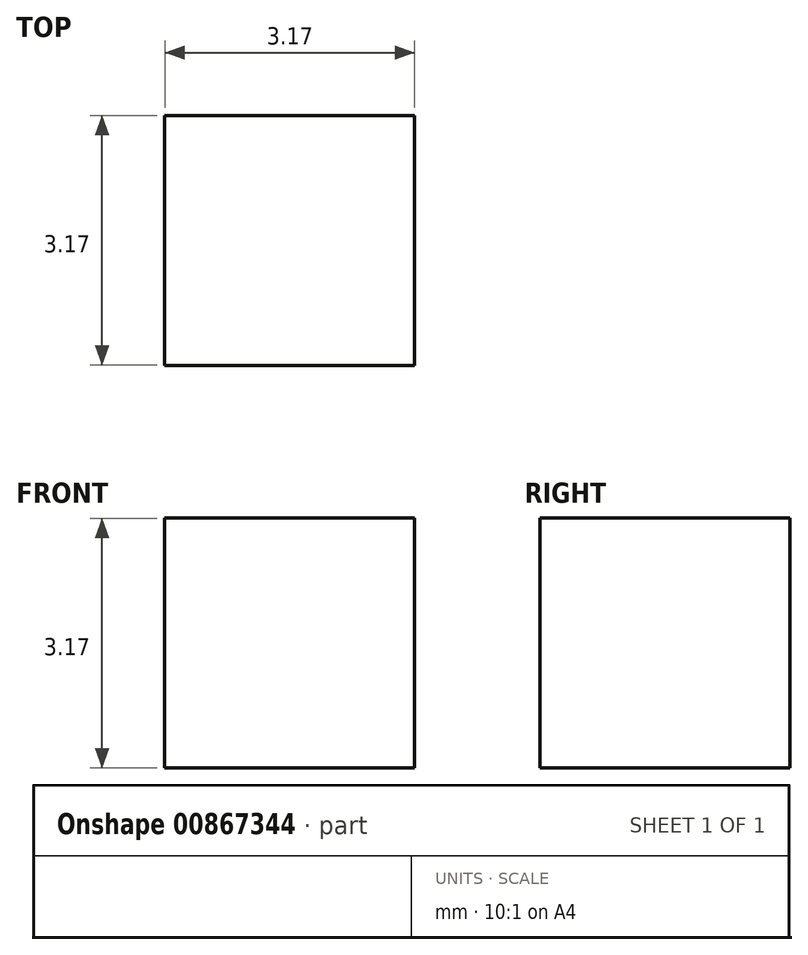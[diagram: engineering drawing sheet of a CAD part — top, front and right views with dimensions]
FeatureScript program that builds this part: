
annotation { "Feature Type Name" : "Feature", "Feature Type Description" : "" }
export const myFeature = defineFeature(function(context is Context, id is Id, definition is map)
    precondition{}
    {
        {
            var Q0;
            Q0=qCreatedBy(makeId("Top.planeOp"),FACE);
            var sketch = newSketch(context, id + "F0", { "sketchPlane" : qUnion([Q0])});
            skLineSegment(sketch, "E0.bottom", {"start": v(-1.3, 0.21) * mm, "end": v(1.87, 0.21) * mm});
            skLineSegment(sketch, "E0.top", {"start": v(-1.3, -2.96) * mm, "end": v(1.87, -2.96) * mm});
            skLineSegment(sketch, "E0.left", {"start": v(-1.3, 0.21) * mm, "end": v(-1.3, -2.96) * mm});
            skLineSegment(sketch, "E0.right", {"start": v(1.87, 0.21) * mm, "end": v(1.87, -2.96) * mm});
            skSolve(sketch);
        }
        {
            var Q0;
            Q0=makeQuery(id+"F0.imprint","IMPRINT",FACE,{"disambiguationData":[TD([[makeQuery(id+"F0.imprint","IMPRINT",EDGE,{"derivedFrom":sQuery(id+"F0.wireOp",EDGE,"E0.bottom")}),-1.0]])]});
            extrude(context, id + "F1", {"entities" : qUnion([Q0]), "depth" : 3.17 * mm, "offsetDistance" : 25.4 * mm});
        }
    });
